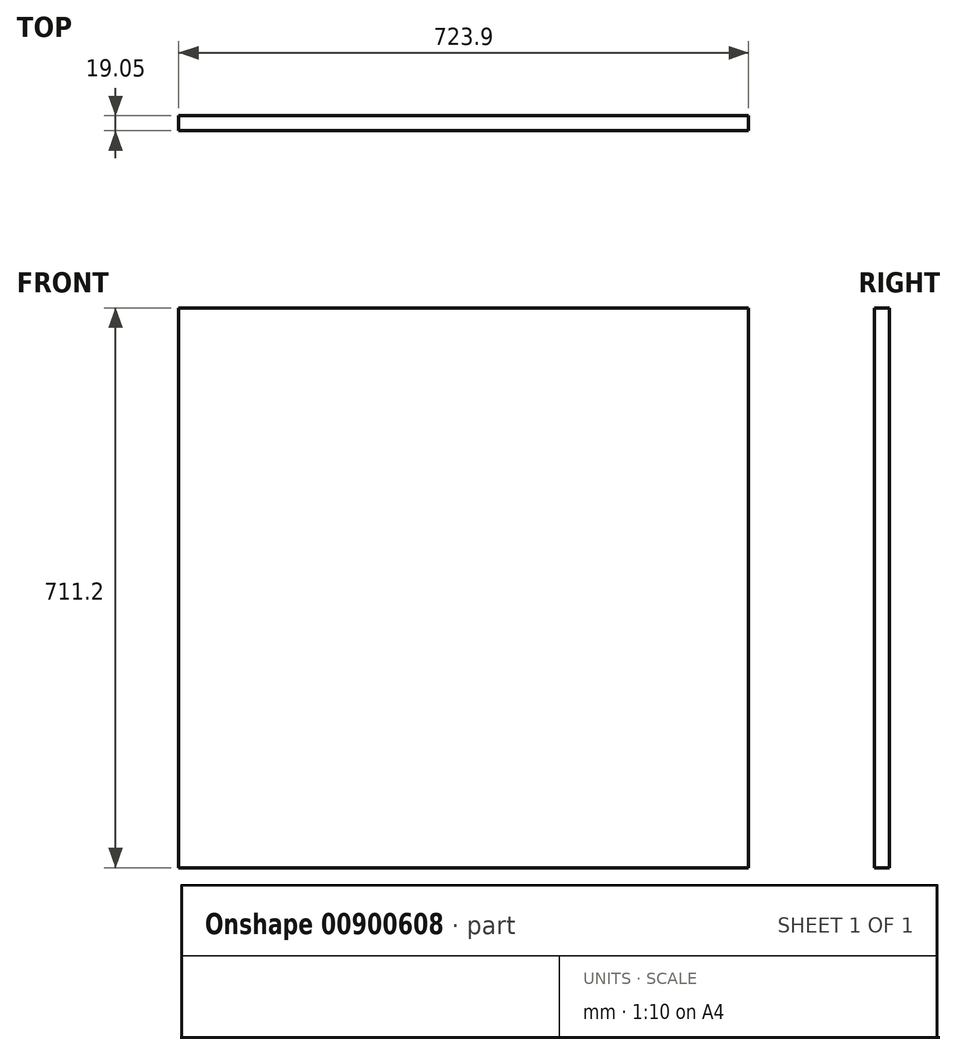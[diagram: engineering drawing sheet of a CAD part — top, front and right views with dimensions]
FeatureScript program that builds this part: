
annotation { "Feature Type Name" : "Feature", "Feature Type Description" : "" }
export const myFeature = defineFeature(function(context is Context, id is Id, definition is map)
    precondition{}
    {
        {
            var Q0;
            Q0=qCreatedBy(makeId("Front.planeOp"),FACE);
            var sketch = newSketch(context, id + "F0", { "sketchPlane" : qUnion([Q0])});
            skLineSegment(sketch, "E0.bottom", {"start": v(361.95, 355.6) * mm, "end": v(-361.95, 355.6) * mm});
            skLineSegment(sketch, "E0.top", {"start": v(361.95, -355.6) * mm, "end": v(-361.95, -355.6) * mm});
            skLineSegment(sketch, "E0.left", {"start": v(361.95, 355.6) * mm, "end": v(361.95, -355.6) * mm});
            skLineSegment(sketch, "E0.right", {"start": v(-361.95, 355.6) * mm, "end": v(-361.95, -355.6) * mm});
            skPoint(sketch, "E0.middle", {"position": v(0, 0) * mm});
            skSolve(sketch);
        }
        {
            var Q0;
            Q0=makeQuery(id+"F0.imprint","IMPRINT",FACE,{"disambiguationData":[TD([[makeQuery(id+"F0.imprint","IMPRINT",EDGE,{"derivedFrom":sQuery(id+"F0.wireOp",EDGE,"E0.bottom")}),1.0]])]});
            extrude(context, id + "F1", {"entities" : qUnion([Q0]), "depth" : 19.05 * mm, "offsetDistance" : 25.4 * mm});
        }
    });
